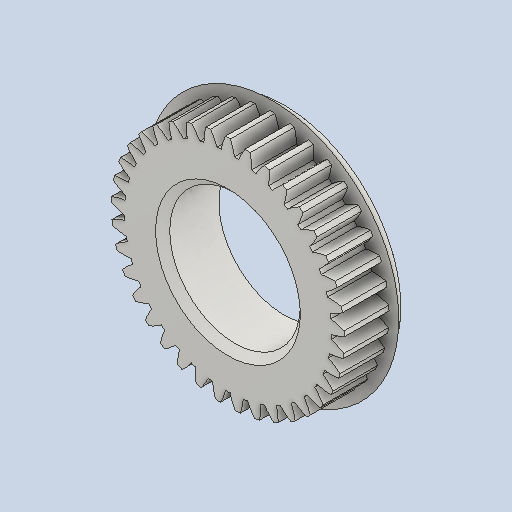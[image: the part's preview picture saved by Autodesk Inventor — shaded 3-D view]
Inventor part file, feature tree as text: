
AUTODESK INVENTOR PART (.ipt)
format: ipt  version: 2022 (Build 260153000, 153)  size: 610,816 bytes
history: native  units: in
note: dims shown in document units (in); Inventor stores cm internally (conversion verified against a paired STEP export)
features: other x12, sketch x4, plane x3
ambient origin geometry x8: Origin, YZ Plane, XZ Plane, XY Plane, X Axis, Y Axis, Z Axis, Center Point
bodies: Solid1 (feature_tree)
feature tree (19):
  other  "Spur Gear2"
  other  "Solid1::Spur Gear2"
  other  "TaggingFeature1"
  sketch  "Sketch1"  dims[d0=0.3937in]
  sketch  "Sketch2"  dims[d9=0.0in d14=0.0in d15=0.9352in d16=0.0in d17=0.0in d18=0.0in d19=0.9352in]
  sketch  "Sketch3"
  sketch  "Sketch4"
  plane  "XZ Plane_1"
  plane  "Work Plane2"
  plane  "Work Plane3"
  other  "Srf1"
  other  "Srf1::Derived"
  other  "Start plane iMate"
  other  "Distance iMate"
  other  "Position iMate"
  other  "Mesh iMate"
  other  "Axis iMate"
  other  "Mesh iMate2"
  other  "Align iMate"
